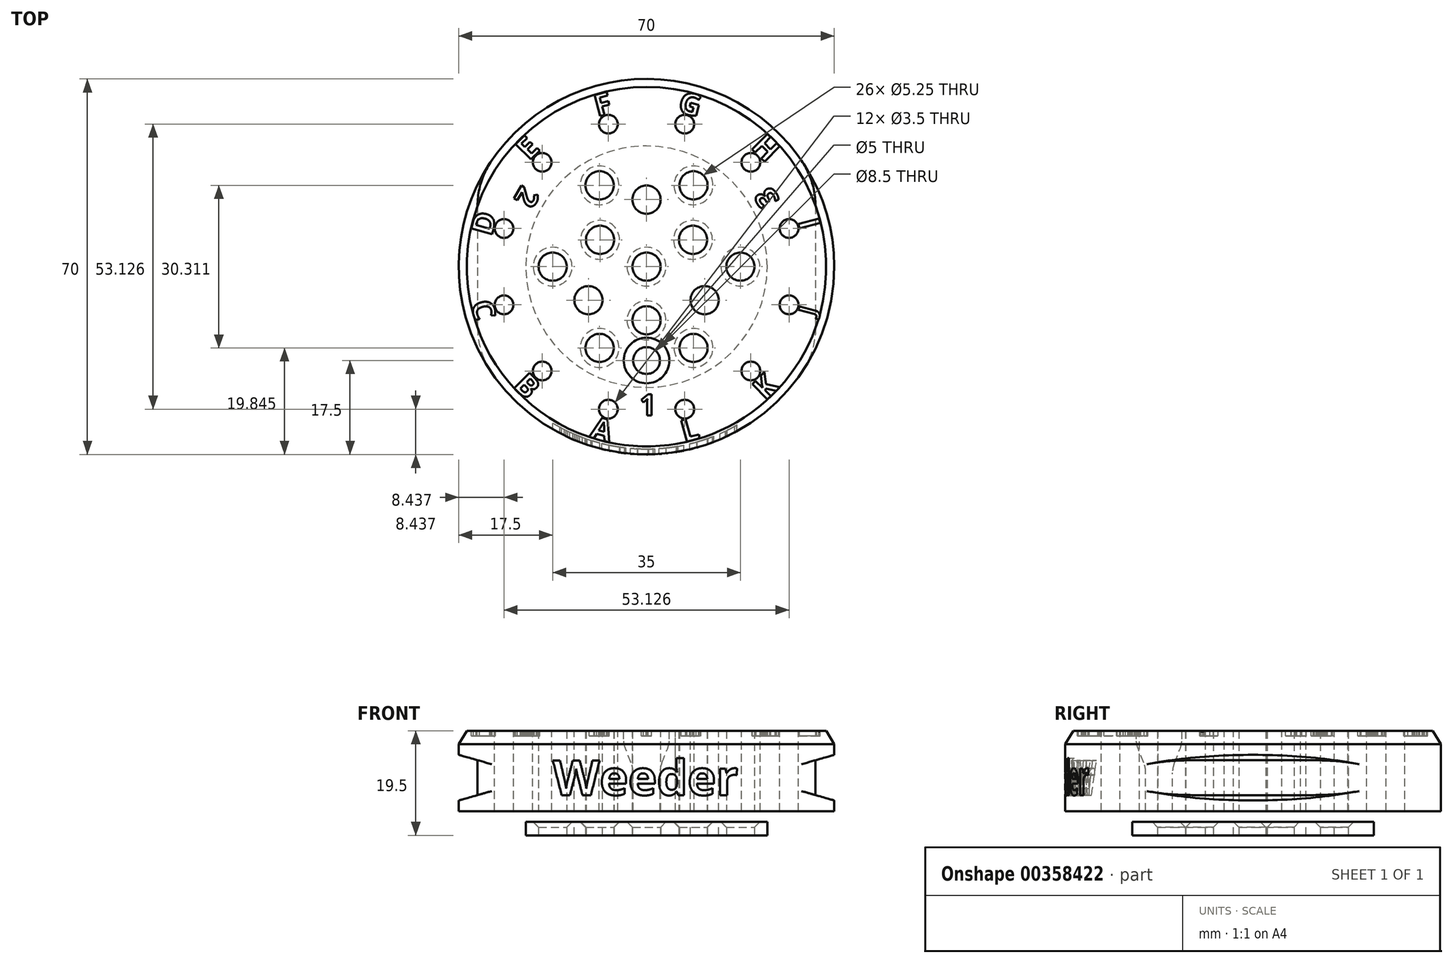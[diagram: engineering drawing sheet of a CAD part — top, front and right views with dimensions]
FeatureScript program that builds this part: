
annotation { "Feature Type Name" : "Feature", "Feature Type Description" : "" }
export const myFeature = defineFeature(function(context is Context, id is Id, definition is map)
    precondition{}
    {
        {
            var Q0;
            Q0=qCreatedBy(makeId("Top.planeOp"),FACE);
            var sketch = newSketch(context, id + "F0", { "sketchPlane" : qUnion([Q0])});
            skCircle(sketch, "E0", {"center": v(0, 0) * mm, "radius": 35 * mm});
            skSolve(sketch);
        }
        {
            var Q0;
            Q0=qSketchRegion(id+"F0",true);
            extrude(context, id + "F1", {"entities" : qUnion([Q0]), "depth" : 15 * mm});
        }
        {
            var Q0;
            Q0=qCreatedBy(makeId("Front.planeOp"),FACE);
            var sketch = newSketch(context, id + "F2", { "sketchPlane" : qUnion([Q0])});
            skText(sketch, "E1", { "text": "Weeder", "fontName": "OpenSans-Bold.ttf"});
            const initialGuessF2  = {"E1": [-0.01747, 0.003, 1, 0, 0.0065]};
            skSetInitialGuess(sketch, initialGuessF2);
            skSolve(sketch);
        }
        {
            var Q0;
            Q0=qSketchRegion(id+"F2",true);
            var Q1;
            Q1=makeQuery(id+"F1.opExtrude","SWEPT_FACE",FACE,{"disambiguationData":[OSD([sQuery(id+"F0.wireOp",EDGE,"E0")])]});
            extrude(context, id + "F3", {"entities" : qUnion([Q0]), "operationType" : NewBodyOperationType.REMOVE, "endBound" : BoundingType.THROUGH_ALL, "endBoundEntityFace" : qUnion([Q1]), "depth" : 25 * mm});
        }
        {
            var Q0;
            Q0=makeQuery(id+"F1.opExtrude","CAP_FACE",FACE,{"disambiguationData":[OSD([sQuery(id+"F0.wireOp",EDGE,"E0")])],"isStart":false});
            var sketch = newSketch(context, id + "F4", { "sketchPlane" : qUnion([Q0])});
            skCircle(sketch, "E2", {"center": v(0, 0) * mm, "radius": 34 * mm});
            skSolve(sketch);
        }
        {
            var Q0;
            Q0=qSketchRegion(id+"F4",true);
            var Q1;
            Q1=makeQuery(id+"F1.opExtrude","CAP_FACE",FACE,{"disambiguationData":[OSD([sQuery(id+"F0.wireOp",EDGE,"E0")])],"isStart":true});
            extrude(context, id + "F5", {"entities" : qUnion([Q0]), "operationType" : NewBodyOperationType.ADD, "endBound" : BoundingType.UP_TO_SURFACE, "oppositeDirection" : true, "endBoundEntityFace" : qUnion([Q1]), "depth" : 25 * mm});
        }
        {
            var Q0;
            Q0=qCreatedBy(makeId("Front.planeOp"),FACE);
            var sketch = newSketch(context, id + "F6", { "sketchPlane" : qUnion([Q0])});
            skLineSegment(sketch, "E3", {"start": v(-35, 10.5) * mm, "end": v(-35, 2) * mm});
            skLineSegment(sketch, "E4", {"start": v(-35, 2) * mm, "end": v(-31.5, 3) * mm});
            skLineSegment(sketch, "E5", {"start": v(-31.5, 3) * mm, "end": v(-31.5, 9.5) * mm});
            skLineSegment(sketch, "E6", {"start": v(-31.5, 9.5) * mm, "end": v(-35, 10.5) * mm});
            skLineSegment(sketch, "E7.MirrorCS", {"start": v(35, 10.5) * mm, "end": v(35, 2) * mm});
            skLineSegment(sketch, "E8.MirrorCS", {"start": v(31.5, 9.5) * mm, "end": v(35, 10.5) * mm});
            skLineSegment(sketch, "E9.MirrorCS", {"start": v(35, 2) * mm, "end": v(31.5, 3) * mm});
            skLineSegment(sketch, "E10.MirrorCS", {"start": v(31.5, 3) * mm, "end": v(31.5, 9.5) * mm});
            skSolve(sketch);
        }
        {
            var Q0;
            Q0=qSketchRegion(id+"F6",true);
            extrude(context, id + "F7", {"entities" : qUnion([Q0]), "operationType" : NewBodyOperationType.REMOVE, "endBound" : BoundingType.THROUGH_ALL, "oppositeDirection" : true, "depth" : 25 * mm, "hasSecondDirection" : true, "secondDirectionBound" : BoundingType.THROUGH_ALL, "secondDirectionOppositeDirection" : false, "secondDirectionDepth" : 25 * mm});
        }
        {
            var Q0;
            {var subQ0=sQuery(id+"F0.wireOp",EDGE,"E0");Q0=makeQuery(id+"F7.boolean.opBoolean","INTERSECT",EDGE,{"disambiguationData":[OD(0.0)],"derivedFrom":[makeQuery(id+"F3.boolean.opBoolean","SPLIT",FACE,{"disambiguationData":[TD([makeQuery(id+"F1.opExtrude","CAP_FACE",FACE,{"disambiguationData":[OSD([subQ0])],"isStart":true})])],"derivedFrom":makeQuery(id+"F1.opExtrude","SWEPT_FACE",FACE,{"disambiguationData":[OSD([subQ0])]})}),makeQuery(id+"F7.opExtrude","SWEPT_FACE",FACE,{"disambiguationData":[OSD([sQuery(id+"F6.wireOp",EDGE,"E5")])]})]});}
            var Q1;
            {var subQ0=sQuery(id+"F0.wireOp",EDGE,"E0");Q1=makeQuery(id+"F7.boolean.opBoolean","INTERSECT",EDGE,{"disambiguationData":[OD(0.0)],"derivedFrom":[makeQuery(id+"F3.boolean.opBoolean","SPLIT",FACE,{"disambiguationData":[TD([makeQuery(id+"F1.opExtrude","CAP_FACE",FACE,{"disambiguationData":[OSD([subQ0])],"isStart":true})])],"derivedFrom":makeQuery(id+"F1.opExtrude","SWEPT_FACE",FACE,{"disambiguationData":[OSD([subQ0])]})}),makeQuery(id+"F7.opExtrude","SWEPT_FACE",FACE,{"disambiguationData":[OSD([sQuery(id+"F6.wireOp",EDGE,"E10.MirrorCS")])]})]});}
            var Q2;
            {var subQ0=sQuery(id+"F0.wireOp",EDGE,"E0");Q2=makeQuery(id+"F7.boolean.opBoolean","INTERSECT",EDGE,{"disambiguationData":[OD(1.0)],"derivedFrom":[makeQuery(id+"F3.boolean.opBoolean","SPLIT",FACE,{"disambiguationData":[TD([makeQuery(id+"F1.opExtrude","CAP_FACE",FACE,{"disambiguationData":[OSD([subQ0])],"isStart":true})])],"derivedFrom":makeQuery(id+"F1.opExtrude","SWEPT_FACE",FACE,{"disambiguationData":[OSD([subQ0])]})}),makeQuery(id+"F7.opExtrude","SWEPT_FACE",FACE,{"disambiguationData":[OSD([sQuery(id+"F6.wireOp",EDGE,"E10.MirrorCS")])]})]});}
            var Q3;
            {var subQ0=sQuery(id+"F0.wireOp",EDGE,"E0");Q3=makeQuery(id+"F7.boolean.opBoolean","INTERSECT",EDGE,{"disambiguationData":[OD(1.0)],"derivedFrom":[makeQuery(id+"F3.boolean.opBoolean","SPLIT",FACE,{"disambiguationData":[TD([makeQuery(id+"F1.opExtrude","CAP_FACE",FACE,{"disambiguationData":[OSD([subQ0])],"isStart":true})])],"derivedFrom":makeQuery(id+"F1.opExtrude","SWEPT_FACE",FACE,{"disambiguationData":[OSD([subQ0])]})}),makeQuery(id+"F7.opExtrude","SWEPT_FACE",FACE,{"disambiguationData":[OSD([sQuery(id+"F6.wireOp",EDGE,"E5")])]})]});}
            fillet(context, id + "F8", {"entities" : qUnion([Q0, Q1, Q2, Q3]), "radius" : 15 * mm, "tangentPropagation" : true, "allowEdgeOverflow" : false});
        }
        {
            var Q0;
            Q0=makeQuery(id+"F1.opExtrude","CAP_FACE",FACE,{"disambiguationData":[OSD([sQuery(id+"F0.wireOp",EDGE,"E0")])],"isStart":false});
            var sketch = newSketch(context, id + "F9", { "sketchPlane" : qUnion([Q0])});
            skCircle(sketch, "E11", {"center": v(0, 12.5) * mm, "radius": 2.62 * mm});
            skCircle(sketch, "E12.1.0", {"center": v(-10.83, -6.25) * mm, "radius": 2.62 * mm});
            skCircle(sketch, "E12.2.0", {"center": v(10.83, -6.25) * mm, "radius": 2.62 * mm});
            skPoint(sketch, "E12.center", {"position": v(0, 0) * mm});
            skCircle(sketch, "E13", {"center": v(0, 0) * mm, "radius": 12.5 * mm, "construction": true});
            skSolve(sketch);
        }
        {
            var Q0;
            Q0=qSketchRegion(id+"F9",true);
            extrude(context, id + "F10", {"entities" : qUnion([Q0]), "operationType" : NewBodyOperationType.REMOVE, "endBound" : BoundingType.THROUGH_ALL, "oppositeDirection" : true, "depth" : 25 * mm});
        }
        {
            var Q0;
            Q0=makeQuery(id+"F1.opExtrude","CAP_FACE",FACE,{"disambiguationData":[OSD([sQuery(id+"F0.wireOp",EDGE,"E0")])],"isStart":false});
            var sketch = newSketch(context, id + "F11", { "sketchPlane" : qUnion([Q0])});
            skCircle(sketch, "E14", {"center": v(0, -17.5) * mm, "radius": 2.5 * mm});
            skCircle(sketch, "E15", {"center": v(0, 0) * mm, "radius": 17.5 * mm, "construction": true});
            skSolve(sketch);
        }
        {
            var Q0;
            Q0=qSketchRegion(id+"F11",true);
            extrude(context, id + "F12", {"entities" : qUnion([Q0]), "operationType" : NewBodyOperationType.REMOVE, "endBound" : BoundingType.THROUGH_ALL, "oppositeDirection" : true, "depth" : 25 * mm});
        }
        {
            var Q0;
            Q0=makeQuery(id+"F1.opExtrude","CAP_FACE",FACE,{"disambiguationData":[OSD([sQuery(id+"F0.wireOp",EDGE,"E0")])],"isStart":false});
            var sketch = newSketch(context, id + "F13", { "sketchPlane" : qUnion([Q0])});
            skCircle(sketch, "E16", {"center": v(0, -17.5) * mm, "radius": 4.25 * mm});
            skSolve(sketch);
        }
        {
            var Q0;
            Q0=qSketchRegion(id+"F13",true);
            extrude(context, id + "F14", {"entities" : qUnion([Q0]), "operationType" : NewBodyOperationType.REMOVE, "oppositeDirection" : true, "depth" : 7.5 * mm});
        }
        {
            var Q0;
            Q0=makeQuery(id+"F14.boolean.opBoolean","COPY",EDGE,{"derivedFrom":makeQuery(id+"F14.opExtrude","CAP_EDGE",EDGE,{"disambiguationData":[OSD([sQuery(id+"F13.wireOp",EDGE,"E16")])],"isStart":false})});
            chamfer(context, id + "F15", {"entities" : qUnion([Q0]), "chamferType" : ChamferType.TWO_OFFSETS, "width1" : 5 * mm, "oppositeDirection" : true, "width2" : 2 * mm, "tangentPropagation" : true});
        }
        {
            var Q0;
            {var subQ0=sQuery(id+"F13.wireOp",EDGE,"E16");Q0=makeQuery(id+"F15.opChamfer","BLEND_EDGE",EDGE,{"blendedFrom":[makeQuery(id+"F14.boolean.opBoolean","COPY",EDGE,{"derivedFrom":makeQuery(id+"F14.opExtrude","CAP_EDGE",EDGE,{"disambiguationData":[OSD([subQ0])],"isStart":false})}),makeQuery(id+"F14.boolean.opBoolean","COPY",FACE,{"derivedFrom":makeQuery(id+"F14.opExtrude","SWEPT_FACE",FACE,{"disambiguationData":[OSD([subQ0])]})})],"blendedInto":[makeQuery(id+"F14.boolean.opBoolean","COPY",FACE,{"derivedFrom":makeQuery(id+"F14.opExtrude","SWEPT_FACE",FACE,{"disambiguationData":[OSD([subQ0])]})})]});}
            var Q1;
            Q1=makeQuery(id+"F15.opChamfer","BLEND_EDGE",EDGE,{"blendedFrom":[makeQuery(id+"F14.boolean.opBoolean","COPY",EDGE,{"derivedFrom":makeQuery(id+"F14.opExtrude","CAP_EDGE",EDGE,{"disambiguationData":[OSD([sQuery(id+"F13.wireOp",EDGE,"E16")])],"isStart":false})}),makeQuery(id+"F12.boolean.opBoolean","COPY",FACE,{"derivedFrom":makeQuery(id+"F12.opExtrude","SWEPT_FACE",FACE,{"disambiguationData":[OSD([sQuery(id+"F11.wireOp",EDGE,"E14")])]})})],"blendedInto":[makeQuery(id+"F12.boolean.opBoolean","COPY",FACE,{"derivedFrom":makeQuery(id+"F12.opExtrude","SWEPT_FACE",FACE,{"disambiguationData":[OSD([sQuery(id+"F11.wireOp",EDGE,"E14")])]})})]});
            fillet(context, id + "F16", {"entities" : qUnion([Q0, Q1]), "radius" : 5 * mm, "tangentPropagation" : true, "allowEdgeOverflow" : false});
        }
        {
            var Q0;
            Q0=makeQuery(id+"F1.opExtrude","CAP_FACE",FACE,{"disambiguationData":[OSD([sQuery(id+"F0.wireOp",EDGE,"E0")])],"isStart":false});
            var sketch = newSketch(context, id + "F17", { "sketchPlane" : qUnion([Q0])});
            skCircle(sketch, "E17", {"center": v(19.45, 19.45) * mm, "radius": 1.75 * mm});
            skCircle(sketch, "E18", {"center": v(0, 0) * mm, "radius": 27.5 * mm, "construction": true});
            skLineSegment(sketch, "E19", {"start": v(0, 0) * mm, "end": v(19.45, 19.45) * mm, "construction": true});
            skCircle(sketch, "E20.1.1", {"center": v(7.12, 26.56) * mm, "radius": 1.75 * mm});
            skCircle(sketch, "E20.2.1", {"center": v(-7.12, 26.56) * mm, "radius": 1.75 * mm});
            skCircle(sketch, "E20.3.1", {"center": v(-19.45, 19.45) * mm, "radius": 1.75 * mm});
            skCircle(sketch, "E20.4.1", {"center": v(-26.56, 7.12) * mm, "radius": 1.75 * mm});
            skCircle(sketch, "E20.5.1", {"center": v(-26.56, -7.12) * mm, "radius": 1.75 * mm});
            skCircle(sketch, "E20.6.1", {"center": v(-19.45, -19.45) * mm, "radius": 1.75 * mm});
            skCircle(sketch, "E20.7.1", {"center": v(-7.12, -26.56) * mm, "radius": 1.75 * mm});
            skCircle(sketch, "E20.8.1", {"center": v(7.12, -26.56) * mm, "radius": 1.75 * mm});
            skCircle(sketch, "E20.9.1", {"center": v(19.45, -19.45) * mm, "radius": 1.75 * mm});
            skCircle(sketch, "E20.10.1", {"center": v(26.56, -7.12) * mm, "radius": 1.75 * mm});
            skCircle(sketch, "E20.11.1", {"center": v(26.56, 7.12) * mm, "radius": 1.75 * mm});
            skSolve(sketch);
        }
        {
            var Q0;
            Q0=qSketchRegion(id+"F17",true);
            extrude(context, id + "F18", {"entities" : qUnion([Q0]), "operationType" : NewBodyOperationType.REMOVE, "endBound" : BoundingType.THROUGH_ALL, "oppositeDirection" : true, "depth" : 25 * mm});
        }
        {
            var Q0;
            Q0=makeQuery(id+"F1.opExtrude","CAP_EDGE",EDGE,{"disambiguationData":[OSD([sQuery(id+"F0.wireOp",EDGE,"E0")])],"isStart":false});
            chamfer(context, id + "F19", {"entities" : qUnion([Q0]), "chamferType" : ChamferType.TWO_OFFSETS, "width1" : 2.5 * mm, "oppositeDirection" : true, "width2" : 1.5 * mm, "tangentPropagation" : true});
        }
        {
            var Q0;
            Q0=makeQuery(id+"F1.opExtrude","CAP_FACE",FACE,{"disambiguationData":[OSD([sQuery(id+"F0.wireOp",EDGE,"E0")])],"isStart":false});
            var sketch = newSketch(context, id + "F20", { "sketchPlane" : qUnion([Q0])});
            skText(sketch, "E21", { "text": "A", "fontName": "OpenSans-Bold.ttf"});
            skText(sketch, "E22", { "text": "B", "fontName": "OpenSans-Bold.ttf"});
            skText(sketch, "E23", { "text": "C", "fontName": "OpenSans-Bold.ttf"});
            skText(sketch, "E24", { "text": "E", "fontName": "OpenSans-Bold.ttf"});
            skText(sketch, "E25", { "text": "F", "fontName": "OpenSans-Bold.ttf"});
            skText(sketch, "E26", { "text": "G", "fontName": "OpenSans-Bold.ttf"});
            skText(sketch, "E27", { "text": "H", "fontName": "OpenSans-Bold.ttf"});
            skText(sketch, "E28", { "text": "I", "fontName": "OpenSans-Bold.ttf"});
            skText(sketch, "E29", { "text": "J", "fontName": "OpenSans-Bold.ttf"});
            skText(sketch, "E30", { "text": "K", "fontName": "OpenSans-Bold.ttf"});
            skText(sketch, "E31", { "text": "L", "fontName": "OpenSans-Bold.ttf"});
            skText(sketch, "E32", { "text": "D", "fontName": "OpenSans-Bold.ttf"});
            skCircle(sketch, "E33", {"center": v(0, 0) * mm, "radius": 29.38 * mm, "construction": true});
            skText(sketch, "E34", { "text": "1", "fontName": "OpenSans-Bold.ttf"});
            skText(sketch, "E35", { "text": "2", "fontName": "OpenSans-Bold.ttf"});
            skText(sketch, "E36", { "text": "3", "fontName": "OpenSans-Bold.ttf"});
            skCircle(sketch, "E37", {"center": v(0, 0) * mm, "radius": 23.75 * mm, "construction": true});
            const initialGuessF20  = {"E21": [-0.0107, -0.03174, 0.96593, -0.25882, 0.00406], "E22": [-0.025, -0.02228, 0.7071, -0.7071, 0.00406], "E23": [-0.03278, -0.00684, 0.25882, -0.96593, 0.00406], "E24": [-0.0219, 0.01964, 0.7071, 0.7071, 0.00406], "E25": [-0.00914, 0.02796, 0.96593, 0.25882, 0.00406], "E26": [0.00567, 0.0289, 0.96593, -0.25882, 0.00406], "E27": [0.0193, 0.02225, 0.7071, -0.7071, 0.00406], "E28": [0.02815, 0.00844, 0.25882, -0.96593, 0.00406], "E29": [0.0313, -0.00927, 0.25882, 0.96593, 0.00325], "E30": [0.02219, -0.0251, 0.7071, 0.7071, 0.00406], "E31": [0.00703, -0.03273, 0.96593, 0.25882, 0.00406], "E32": [-0.02892, 0.00557, 0.25882, 0.96593, 0.00406], "E34": [-0.00133, -0.02775, 1, 0, 0.004], "E35": [-0.0232, 0.01533, -0.5, -0.86603, 0.004], "E36": [0.02486, 0.01244, -0.5, 0.86603, 0.004]};
            skSetInitialGuess(sketch, initialGuessF20);
            skSolve(sketch);
        }
        {
            var Q0;
            Q0=qSketchRegion(id+"F20",true);
            extrude(context, id + "F21", {"entities" : qUnion([Q0]), "operationType" : NewBodyOperationType.REMOVE, "oppositeDirection" : true, "depth" : 1 * mm});
        }
        {
            var Q0;
            Q0=makeQuery(id+"F1.opExtrude","CAP_FACE",FACE,{"disambiguationData":[OSD([sQuery(id+"F0.wireOp",EDGE,"E0")])],"isStart":true});
            cPlane(context, id + "F22", {"entities" : qUnion([Q0]), "cplaneType" : CPlaneType.OFFSET, "offset" : 2 * mm, "width" : 150 * mm, "height" : 150 * mm});
        }
        {
            var Q0;
            Q0=qCreatedBy(id+"F22.planeOp",FACE);
            var sketch = newSketch(context, id + "F23", { "sketchPlane" : qUnion([Q0])});
            skCircle(sketch, "E38.0", {"center": v(-10.83, 6.25) * mm, "radius": 2.62 * mm});
            skCircle(sketch, "E38.1", {"center": v(10.83, 6.25) * mm, "radius": 2.62 * mm});
            skCircle(sketch, "E38.2", {"center": v(0, -12.5) * mm, "radius": 2.62 * mm});
            skCircle(sketch, "E39", {"center": v(0, 0) * mm, "radius": 22.5 * mm});
            skSolve(sketch);
        }
        {
            var Q0;
            Q0=qSketchRegion(id+"F23",true);
            extrude(context, id + "F24", {"entities" : qUnion([Q0]), "depth" : 2.5 * mm});
        }
        {
            var Q0;
            Q0=makeQuery(id+"F24.opExtrude","CAP_FACE",FACE,{"disambiguationData":[OSD([sQuery(id+"F23.wireOp",EDGE,"E38.0"),sQuery(id+"F23.wireOp",EDGE,"E38.1"),sQuery(id+"F23.wireOp",EDGE,"E38.2"),sQuery(id+"F23.wireOp",EDGE,"E39")])],"isStart":false});
            var sketch = newSketch(context, id + "F25", { "sketchPlane" : qUnion([Q0])});
            skCircle(sketch, "E40", {"center": v(0, 0) * mm, "radius": 2.62 * mm});
            skCircle(sketch, "E41", {"center": v(0, 10) * mm, "radius": 2.62 * mm});
            skCircle(sketch, "E42.1.0", {"center": v(-8.66, -5) * mm, "radius": 2.62 * mm});
            skCircle(sketch, "E42.2.0", {"center": v(8.66, -5) * mm, "radius": 2.62 * mm});
            skCircle(sketch, "E43", {"center": v(-8.75, 15.16) * mm, "radius": 2.62 * mm});
            skLineSegment(sketch, "E44", {"start": v(-8.75, 15.16) * mm, "end": v(0, 0) * mm, "construction": true});
            skLineSegment(sketch, "E45", {"start": v(0, 0) * mm, "end": v(0, 10) * mm, "construction": true});
            skCircle(sketch, "E46.1.0", {"center": v(-17.5, 0) * mm, "radius": 2.62 * mm});
            skCircle(sketch, "E46.2.0", {"center": v(-8.75, -15.16) * mm, "radius": 2.62 * mm});
            skCircle(sketch, "E46.3.0", {"center": v(8.75, -15.16) * mm, "radius": 2.62 * mm});
            skCircle(sketch, "E46.4.0", {"center": v(17.5, 0) * mm, "radius": 2.62 * mm});
            skCircle(sketch, "E46.5.0", {"center": v(8.75, 15.16) * mm, "radius": 2.62 * mm});
            skSolve(sketch);
        }
        {
            var Q0;
            Q0=qSketchRegion(id+"F25",true);
            extrude(context, id + "F26", {"entities" : qUnion([Q0]), "operationType" : NewBodyOperationType.REMOVE, "endBound" : BoundingType.THROUGH_ALL, "oppositeDirection" : true, "depth" : 25 * mm});
        }
        {
            var Q0;
            Q0=makeQuery(id+"F26.boolean.opBoolean","INTERSECT",EDGE,{"derivedFrom":[makeQuery(id+"F24.opExtrude","CAP_FACE",FACE,{"disambiguationData":[OSD([sQuery(id+"F23.wireOp",EDGE,"E38.0"),sQuery(id+"F23.wireOp",EDGE,"E38.1"),sQuery(id+"F23.wireOp",EDGE,"E38.2"),sQuery(id+"F23.wireOp",EDGE,"E39")])],"isStart":true}),makeQuery(id+"F26.opExtrude","SWEPT_FACE",FACE,{"disambiguationData":[OSD([sQuery(id+"F25.wireOp",EDGE,"E40")])]})]});
            var Q1;
            Q1=makeQuery(id+"F26.boolean.opBoolean","INTERSECT",EDGE,{"derivedFrom":[makeQuery(id+"F24.opExtrude","CAP_FACE",FACE,{"disambiguationData":[OSD([sQuery(id+"F23.wireOp",EDGE,"E38.0"),sQuery(id+"F23.wireOp",EDGE,"E38.1"),sQuery(id+"F23.wireOp",EDGE,"E38.2"),sQuery(id+"F23.wireOp",EDGE,"E39")])],"isStart":true}),makeQuery(id+"F26.opExtrude","SWEPT_FACE",FACE,{"disambiguationData":[OSD([sQuery(id+"F25.wireOp",EDGE,"E41")])]})]});
            var Q2;
            Q2=makeQuery(id+"F26.boolean.opBoolean","INTERSECT",EDGE,{"derivedFrom":[makeQuery(id+"F24.opExtrude","CAP_FACE",FACE,{"disambiguationData":[OSD([sQuery(id+"F23.wireOp",EDGE,"E38.0"),sQuery(id+"F23.wireOp",EDGE,"E38.1"),sQuery(id+"F23.wireOp",EDGE,"E38.2"),sQuery(id+"F23.wireOp",EDGE,"E39")])],"isStart":true}),makeQuery(id+"F26.opExtrude","SWEPT_FACE",FACE,{"disambiguationData":[OSD([sQuery(id+"F25.wireOp",EDGE,"E46.2.0")])]})]});
            var Q3;
            Q3=makeQuery(id+"F26.boolean.opBoolean","INTERSECT",EDGE,{"derivedFrom":[makeQuery(id+"F24.opExtrude","CAP_FACE",FACE,{"disambiguationData":[OSD([sQuery(id+"F23.wireOp",EDGE,"E38.0"),sQuery(id+"F23.wireOp",EDGE,"E38.1"),sQuery(id+"F23.wireOp",EDGE,"E38.2"),sQuery(id+"F23.wireOp",EDGE,"E39")])],"isStart":true}),makeQuery(id+"F26.opExtrude","SWEPT_FACE",FACE,{"disambiguationData":[OSD([sQuery(id+"F25.wireOp",EDGE,"E46.1.0")])]})]});
            var Q4;
            Q4=makeQuery(id+"F26.boolean.opBoolean","INTERSECT",EDGE,{"derivedFrom":[makeQuery(id+"F24.opExtrude","CAP_FACE",FACE,{"disambiguationData":[OSD([sQuery(id+"F23.wireOp",EDGE,"E38.0"),sQuery(id+"F23.wireOp",EDGE,"E38.1"),sQuery(id+"F23.wireOp",EDGE,"E38.2"),sQuery(id+"F23.wireOp",EDGE,"E39")])],"isStart":true}),makeQuery(id+"F26.opExtrude","SWEPT_FACE",FACE,{"disambiguationData":[OSD([sQuery(id+"F25.wireOp",EDGE,"E43")])]})]});
            var Q5;
            Q5=makeQuery(id+"F26.boolean.opBoolean","INTERSECT",EDGE,{"derivedFrom":[makeQuery(id+"F24.opExtrude","CAP_FACE",FACE,{"disambiguationData":[OSD([sQuery(id+"F23.wireOp",EDGE,"E38.0"),sQuery(id+"F23.wireOp",EDGE,"E38.1"),sQuery(id+"F23.wireOp",EDGE,"E38.2"),sQuery(id+"F23.wireOp",EDGE,"E39")])],"isStart":true}),makeQuery(id+"F26.opExtrude","SWEPT_FACE",FACE,{"disambiguationData":[OSD([sQuery(id+"F25.wireOp",EDGE,"E46.5.0")])]})]});
            var Q6;
            Q6=makeQuery(id+"F26.boolean.opBoolean","INTERSECT",EDGE,{"derivedFrom":[makeQuery(id+"F24.opExtrude","CAP_FACE",FACE,{"disambiguationData":[OSD([sQuery(id+"F23.wireOp",EDGE,"E38.0"),sQuery(id+"F23.wireOp",EDGE,"E38.1"),sQuery(id+"F23.wireOp",EDGE,"E38.2"),sQuery(id+"F23.wireOp",EDGE,"E39")])],"isStart":true}),makeQuery(id+"F26.opExtrude","SWEPT_FACE",FACE,{"disambiguationData":[OSD([sQuery(id+"F25.wireOp",EDGE,"E46.4.0")])]})]});
            var Q7;
            Q7=makeQuery(id+"F26.boolean.opBoolean","INTERSECT",EDGE,{"derivedFrom":[makeQuery(id+"F24.opExtrude","CAP_FACE",FACE,{"disambiguationData":[OSD([sQuery(id+"F23.wireOp",EDGE,"E38.0"),sQuery(id+"F23.wireOp",EDGE,"E38.1"),sQuery(id+"F23.wireOp",EDGE,"E38.2"),sQuery(id+"F23.wireOp",EDGE,"E39")])],"isStart":true}),makeQuery(id+"F26.opExtrude","SWEPT_FACE",FACE,{"disambiguationData":[OSD([sQuery(id+"F25.wireOp",EDGE,"E46.3.0")])]})]});
            var Q8;
            Q8=makeQuery(id+"F26.boolean.opBoolean","INTERSECT",EDGE,{"derivedFrom":[makeQuery(id+"F24.opExtrude","CAP_FACE",FACE,{"disambiguationData":[OSD([sQuery(id+"F23.wireOp",EDGE,"E38.0"),sQuery(id+"F23.wireOp",EDGE,"E38.1"),sQuery(id+"F23.wireOp",EDGE,"E38.2"),sQuery(id+"F23.wireOp",EDGE,"E39")])],"isStart":true}),makeQuery(id+"F26.opExtrude","SWEPT_FACE",FACE,{"disambiguationData":[OSD([sQuery(id+"F25.wireOp",EDGE,"E42.1.0")])]})]});
            var Q9;
            Q9=makeQuery(id+"F26.boolean.opBoolean","INTERSECT",EDGE,{"derivedFrom":[makeQuery(id+"F24.opExtrude","CAP_FACE",FACE,{"disambiguationData":[OSD([sQuery(id+"F23.wireOp",EDGE,"E38.0"),sQuery(id+"F23.wireOp",EDGE,"E38.1"),sQuery(id+"F23.wireOp",EDGE,"E38.2"),sQuery(id+"F23.wireOp",EDGE,"E39")])],"isStart":true}),makeQuery(id+"F26.opExtrude","SWEPT_FACE",FACE,{"disambiguationData":[OSD([sQuery(id+"F25.wireOp",EDGE,"E42.2.0")])]})]});
            chamfer(context, id + "F27", {"entities" : qUnion([Q0, Q1, Q2, Q3, Q4, Q5, Q6, Q7, Q8, Q9]), "width" : 1 * mm, "tangentPropagation" : true});
        }
    });
